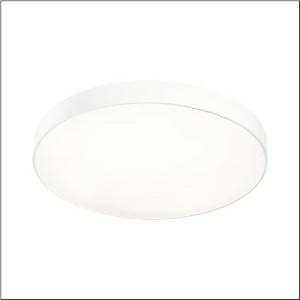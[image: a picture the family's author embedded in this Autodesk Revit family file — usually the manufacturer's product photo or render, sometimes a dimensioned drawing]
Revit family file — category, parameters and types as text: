
# Revit family: round_21_l_51mr38fd0321w
name_source: partatom
category: Lighting Fixtures
units: mm (PartAtom-declared; Revit-internal decimal feet)

## family parameters
Cut with Voids When Loaded = No
Host = Face
Light Source = No
Part Type = Normal
Room Calculation Point = No
Round Connector Dimension = Use Diameter
Shared = No

## types (1)
- Round 21 L (1 x LED, 13590 lm, 97 W, 3000K)
    Apparent Load = 97 VA
    CIE Flux Codes = 49 80 96 100 100
    Color Rendering = 80
    Color Temperature = 3000K
    Default Elevation = 1800 mm
    Description = Round 21 L, wall and ceiling luminaire, primary optical cover: cover, of PMMA, opal, light emission: direct distribution, primary light characteristic: symmetric, installation type: suspended mounting, surface-mounted, LED, rated luminous flux: 13.590lm, luminous efficacy: 140lm/W, light colour: 830, colour temperature: 3000K, control gear: DALI 2, with terminal, 5-pole, mains connection: 230V, AC, 50/60Hz, rated input power: 97W, housing, of aluminium, coated, white, diameter: 850mm, height: 62mm, protection rating (complete): IP40, insulation class (complete): insulation class I (protective earthing), certification: CE, impact resistance: IK04, permissible operating ambient temperature: -10..+35°C, packaging unit: 1 piece
    Height = 87 mm
    Lamp = 1 x LED
    Lamp Light Flux = 13590 lm
    Lamp Power = 97 W
    Lamp count = 1
    Length = 850 mm
    Luminous efficacy = 140 lm/W
    Manufacturer = Siteco
    ModVariant = No
    Model = 51MR38FD0321W
    Mounting Place = Ceiling
    Mounting Type = Surface mounted
    Number of Poles = 1
    OnlyDefault = Yes
    Power Factor = 1
    Product Name = Round 21 L
    Product group = wall and ceiling luminaire | ceiling mounted
    ProductGroupID = 304
    Protection Class = Protection class I
    Protection Degree = IP 40
    RLX_Detail_Level = 1
    RLX_Emergency_Light_Flux = 0 lm
    RLX_Emergency_Type = 0
    RLX_Emergency_Type_DB = No
    RlxData = <blob elided: 15029 chars, md5=55d5e14f>
    Socket = socket
    Standby Power = 0 W
    System Light Flux = 13590 lm
    System Power = 97 W
    Type Comments = Product without accessories
    Type Image = l_1258320.jpg
    URL = http://relux.com
    VarID = ---
    Voltage = 0 V
    Weight = 0.00 kg
    Width = 0 mm  [stored 0 ft]

note: [stored X ft] marks values corroborated as IEEE doubles in the binary element streams (Revit-internal decimal feet)

## geometry (parser evidence)
native form markers: Sweep x11
no freeform markers — native parametric forms only
